# Revit family: Eurolan_Комплект профилей опорных L-типа регулируемых до 100 кг
name_source: partatom
category: Устройства связи
units: mm (PartAtom-declared; Revit-internal decimal feet)

## family parameters
Всегда вертикально = Да
На основе рабочей плоскости = Нет
Общий = Нет
При загрузке вырезать с полостями = Нет
Размер круглого соединителя = Использовать диаметр
Сохранять ориентацию аннотаций = Нет
Тип детали = Нормальный
Точка расчета площади = Нет

## types (3) — shared parameters
ADSK_Единица измерения = шт
ADSK_Завод-изготовитель = Eurolan
ADSK_Количество = 1
ADSK_Марка = L-типа
ADSK_Материал = Оценковка

## per-type parameters (varying)
| type | ADSK_Код изделия | ADSK_Масса | ADSK_Наименование | ADSK_Наименование краткое | Выбор_геометрии |
| Комплект профилей опорных L-типа регулируемых 325 мм_для шкафов глубиной 600 мм | 60A-41-60-09SL | 1.3 | Комплект профилей опорных L-типа регулируемых 325 мм, для шкафов глубиной 600 мм, до 100 кг | Комплект профилей опорных L-типа регулируемых 325 мм | Комплект профилей опорных L-типа регулируемых : 325 |
| Комплект профилей опорных L-типа регулируемых 525 мм_для шкафов глубиной 800 мм | 60A-41-80-09SL | 1.7 | Комплект профилей опорных L-типа регулируемых 525 мм, для шкафов глубиной 800 мм, до 100 кг | Комплект профилей опорных L-типа регулируемых 525 мм | Комплект профилей опорных L-типа регулируемых : 525 |
| Комплект профилей опорных L-типа регулируемых 760 мм_для шкафов глубиной 1000 мм | 60A-41-0A-09SL | 2.3 | Комплект профилей опорных L-типа регулируемых 760 мм, для шкафов глубиной 1000 мм, до 100 кг | Комплект профилей опорных L-типа регулируемых 760 мм | Комплект профилей опорных L-типа регулируемых : 760 |
